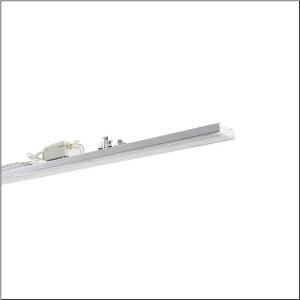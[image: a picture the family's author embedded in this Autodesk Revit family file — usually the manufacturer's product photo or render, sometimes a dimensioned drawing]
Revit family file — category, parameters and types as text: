
# Revit family: licross_21_recessed_mo_52tl1ecn485g
name_source: partatom
category: Lighting Fixtures
units: mm (PartAtom-declared; Revit-internal decimal feet)

## family parameters
Cut with Voids When Loaded = No
Host = Face
Light Source = No
Part Type = Normal
Room Calculation Point = No
Round Connector Dimension = Use Diameter
Shared = No

## types (1)
- --- (1 x LED, 8960 lm, 49.9 W, 4000K)
    Apparent Load = 50 VA
    CIE Flux Codes = 85 95 99 100 100
    Color Rendering = 80
    Color Temperature = 4000K
    Default Elevation = 1800 mm
    Description = Licross 21 Recessed MO, luminaire insert, of sheet steel, galvanised, coil coated, white, length: 1.500mm, width: 66mm, height: 67mm, LED rated luminous flux: 8.960lm, light colour: 840, SDCM (Standard Deviation of Colour Matching)MacAdam ≤ 3 SDCM (initial), control gear: ON/OFF Multilumen, CLOi, with plug, 3-pole, with phase selection, mains connection: 220..240V, AC, 50/60Hz, start of lifetime: 50W, end of service life: 61W, internal wiring halogen-free, primary light control with lens, of plastic, primary optical cover: cover, of PMMA, light emission: direct distribution, primary light characteristic: symmetric, protection rating (complete): IP40, insulation class (complete): insulation class I (protective earthing), certification: CE, ENEC, VDE, UKCA, protection symbol: D if used in an environment without relevant dust loads with corresponding accessories, impact resistance: IK06, permissible ambient temperature for indoor applications: -35..+40°C, corresponds to IFS (International Featured Standards) requirements for safety and quality in the food industry, reducing of maximum allowable ambient temperature of 5°C with ceiling mounting, LABS conformity tested according to VDMA 24364:2018-05, The light source and the operating device comply with the requirements of the Ecodesign Regulation (EU) 2019/2020 and are replaceable in accordance with this regulation, packaging unit: 1 piece
    Height = 58 mm
    Lamp = 1 x LED
    Lamp Light Flux = 8960 lm
    Lamp Power = 49.9 W
    Lamp count = 1
    Length = 1500 mm
    Luminous efficacy = 180 lm/W
    Manufacturer = Siteco
    ModVariant = No
    Model = 52TL1ECN485G
    Mounting Place = Ceiling
    Mounting Type = Pendant
    Number of Poles = 1
    OnlyDefault = Yes
    Power Factor = 1
    Product Name = Licross 21 Recessed MO
    Product group = luminaire insert | ceiling pendant
    ProductGroupID = 901
    Protection Class = Protection class I
    Protection Degree = IP 40
    RLX_Detail_Level = 1
    RLX_Emergency_Light_Flux = 0 lm
    RLX_Emergency_Type = 0
    RLX_Emergency_Type_DB = No
    RlxData = <blob elided: 22613 chars, md5=3511e67a>
    Socket = socket
    Standby Power = 0 W
    System Light Flux = 8960 lm
    System Power = 50 W
    Type Comments = factory setting: luminous flux: 100 % | (A | C | E) | 116 mA
    Type Image = l_1296930.jpg
    URL = http://relux.com
    VarID = @adj_111429
    Voltage = 0 V
    Weight = 0.00 kg
    Width = 66 mm

## geometry (parser evidence)
native form markers: Blend x4, Sweep x10
no freeform markers — native parametric forms only
